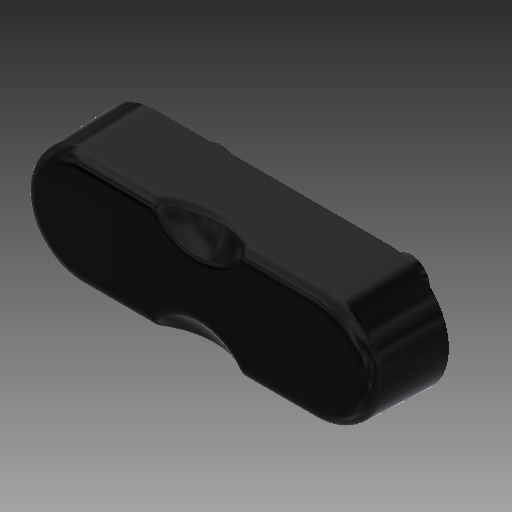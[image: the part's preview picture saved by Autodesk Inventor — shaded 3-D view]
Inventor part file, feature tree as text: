
AUTODESK INVENTOR PART (.ipt)
format: ipt  version: 2019 (Build 230136000, 136)  size: 370,688 bytes
history: native  units: mm
features: sketch x6, rib x3, extrude x2, fillet x2, projected_geometry x2, revolve x1, mirror x1, shell x1, plane x1
ambient origin geometry x8: Origin, YZ Plane, XZ Plane, XY Plane, X Axis, Y Axis, Z Axis, Center Point
bodies: Solid1 (feature_tree)
feature tree (19):
  extrude  "Extrusion1"  Depth=65.0mm
  revolve  "Revolution1"  [1 undecoded]
  mirror  "Mirror2"
  fillet  "Fillet2"  Radius=14.0mm
  fillet  "Fillet3"  Radius=15.0mm
  shell  "Shell1"  Thickness=25.0mm
  plane  "Work Plane2"
  extrude  "Extrusion2"  TaperAngle=90.0deg  [1 undecoded]
  rib  "Rib1"
  rib  "Rib2"
  rib  "Rib3"
  sketch  "Sketch1"  dims[d2=22.0mm d3=65.0mm]
  sketch  "Sketch4"  dims[d4=43.0mm d5=21.5mm d6=14.0mm d7=-0.349066mm d13=15.0mm d14=25.0mm]
  sketch  "Sketch5"  dims[d15=15.0mm d16=90.0deg]
  sketch  "Sketch6"  dims[d18=2.5mm]
  sketch  "Sketch7"  dims[d19=2.0mm]
  projected_geometry  "Projected Loop1"
  sketch  "Sketch8"  dims[d20=1.5mm d21=-8.0mm d22=35.0mm d23=17.5mm d24=7.0mm d25=14.0mm d26=0.174533mm d27=1.0mm d28=1.0mm d29=0.087266mm d30=1.0mm d31=1.0mm d32=0.087266mm d33=1.0mm d34=1.0mm d35=0.087266mm]
  projected_geometry  "Projected Loop2"
note: 2 required parameter values undecoded (feature->parameter linkage not recoverable at this tier; creation-order binding heuristic only, values carry confidence <= 0.55)